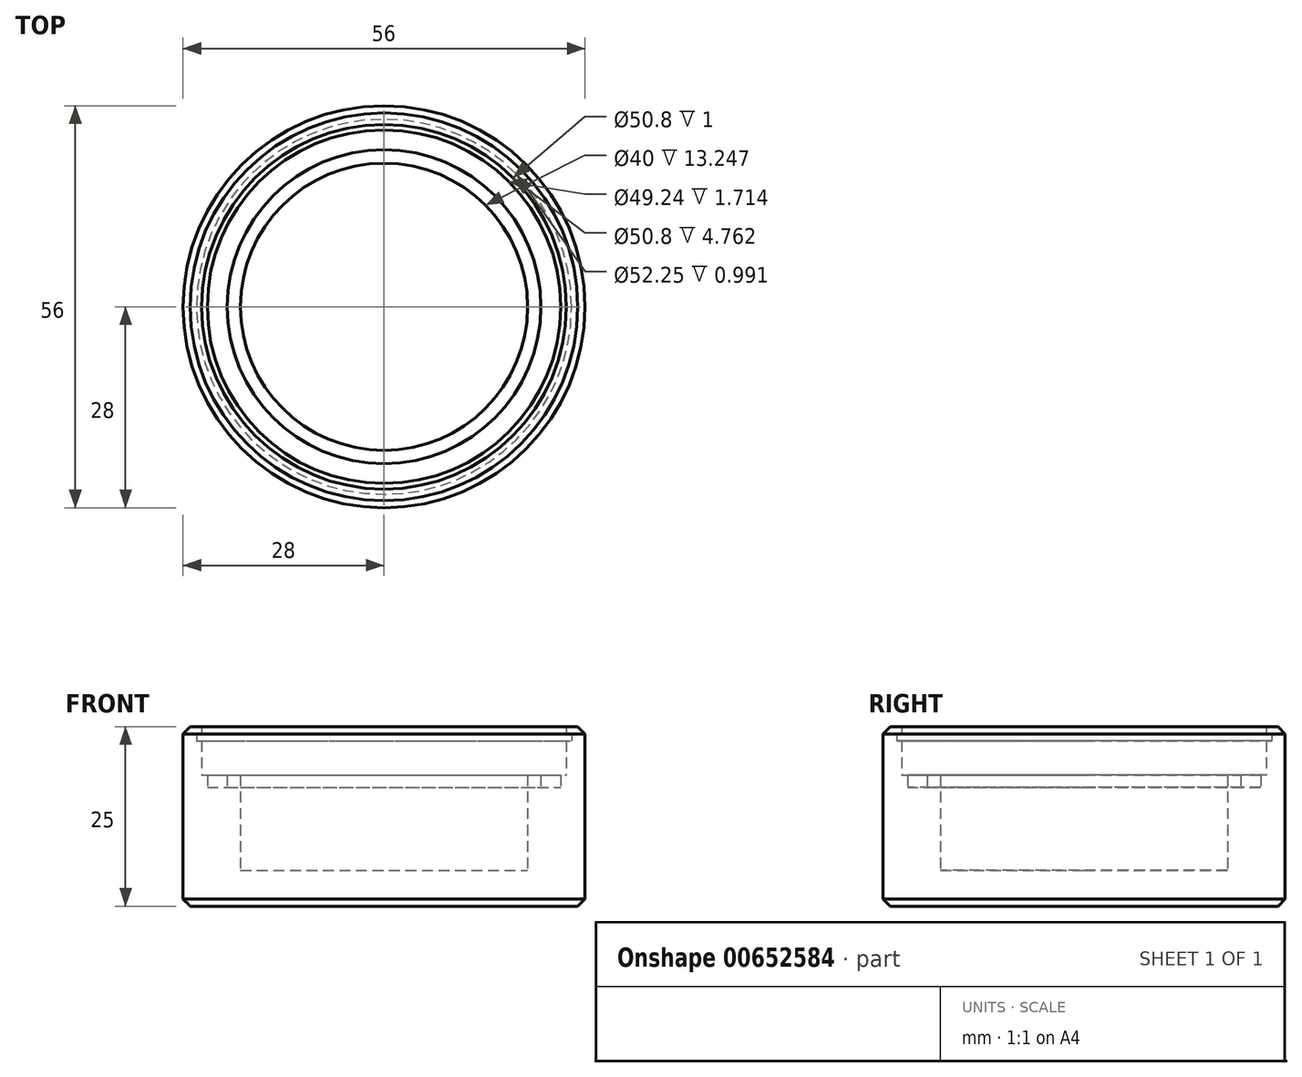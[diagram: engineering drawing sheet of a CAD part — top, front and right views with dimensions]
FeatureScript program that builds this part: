
annotation { "Feature Type Name" : "Feature", "Feature Type Description" : "" }
export const myFeature = defineFeature(function(context is Context, id is Id, definition is map)
    precondition{}
    {
        {
            var Q0;
            Q0=qCreatedBy(makeId("Right.planeOp"),FACE);
            var sketch = newSketch(context, id + "F0", { "sketchPlane" : qUnion([Q0])});
            skLineSegment(sketch, "E0", {"start": v(-25.4, 25) * mm, "end": v(-27, 25) * mm});
            skLineSegment(sketch, "E1", {"start": v(-27, 25) * mm, "end": v(-28, 24) * mm});
            skLineSegment(sketch, "E2", {"start": v(-28, 24) * mm, "end": v(-28, 1) * mm});
            skLineSegment(sketch, "E3", {"start": v(-28, 1) * mm, "end": v(-27, 0) * mm});
            skLineSegment(sketch, "E4", {"start": v(-27, 0) * mm, "end": v(0, 0) * mm});
            skLineSegment(sketch, "E5", {"start": v(0, 0) * mm, "end": v(0, 5) * mm});
            skLineSegment(sketch, "E6", {"start": v(0, 5) * mm, "end": v(-20, 5) * mm});
            skLineSegment(sketch, "E7", {"start": v(-20, 5) * mm, "end": v(-20, 18.25) * mm});
            skLineSegment(sketch, "E8", {"start": v(-20, 18.25) * mm, "end": v(-21.86, 18.25) * mm});
            skLineSegment(sketch, "E9", {"start": v(-21.86, 18.25) * mm, "end": v(-21.86, 16.53) * mm});
            skLineSegment(sketch, "E10", {"start": v(-21.86, 16.53) * mm, "end": v(-24.62, 16.53) * mm});
            skLineSegment(sketch, "E11", {"start": v(-24.62, 16.53) * mm, "end": v(-24.62, 18.25) * mm});
            skLineSegment(sketch, "E12", {"start": v(-24.62, 18.25) * mm, "end": v(-25.4, 18.25) * mm});
            skLineSegment(sketch, "E13", {"start": v(-25.4, 18.25) * mm, "end": v(-25.4, 23) * mm});
            skLineSegment(sketch, "E14", {"start": v(-25.4, 23) * mm, "end": v(-26.12, 23) * mm});
            skLineSegment(sketch, "E15", {"start": v(-26.12, 23) * mm, "end": v(-26.12, 24) * mm});
            skLineSegment(sketch, "E16", {"start": v(-26.12, 24) * mm, "end": v(-25.4, 24) * mm});
            skLineSegment(sketch, "E17", {"start": v(-25.4, 24) * mm, "end": v(-25.4, 25) * mm});
            skSolve(sketch);
        }
        {
            var Q0;
            Q0=makeQuery(id+"F0.imprint","IMPRINT",FACE,{"disambiguationData":[TD([[makeQuery(id+"F0.imprint","IMPRINT",EDGE,{"derivedFrom":sQuery(id+"F0.wireOp",EDGE,"E0")}),1.0]])]});
            var Q1;
            Q1=sQuery(id+"F0.wireOp",EDGE,"E5");
            revolve(context, id + "F1", {"entities" : qUnion([Q0]), "axis" : qUnion([Q1]), "revolveType" : RevolveType.FULL});
        }
    });
